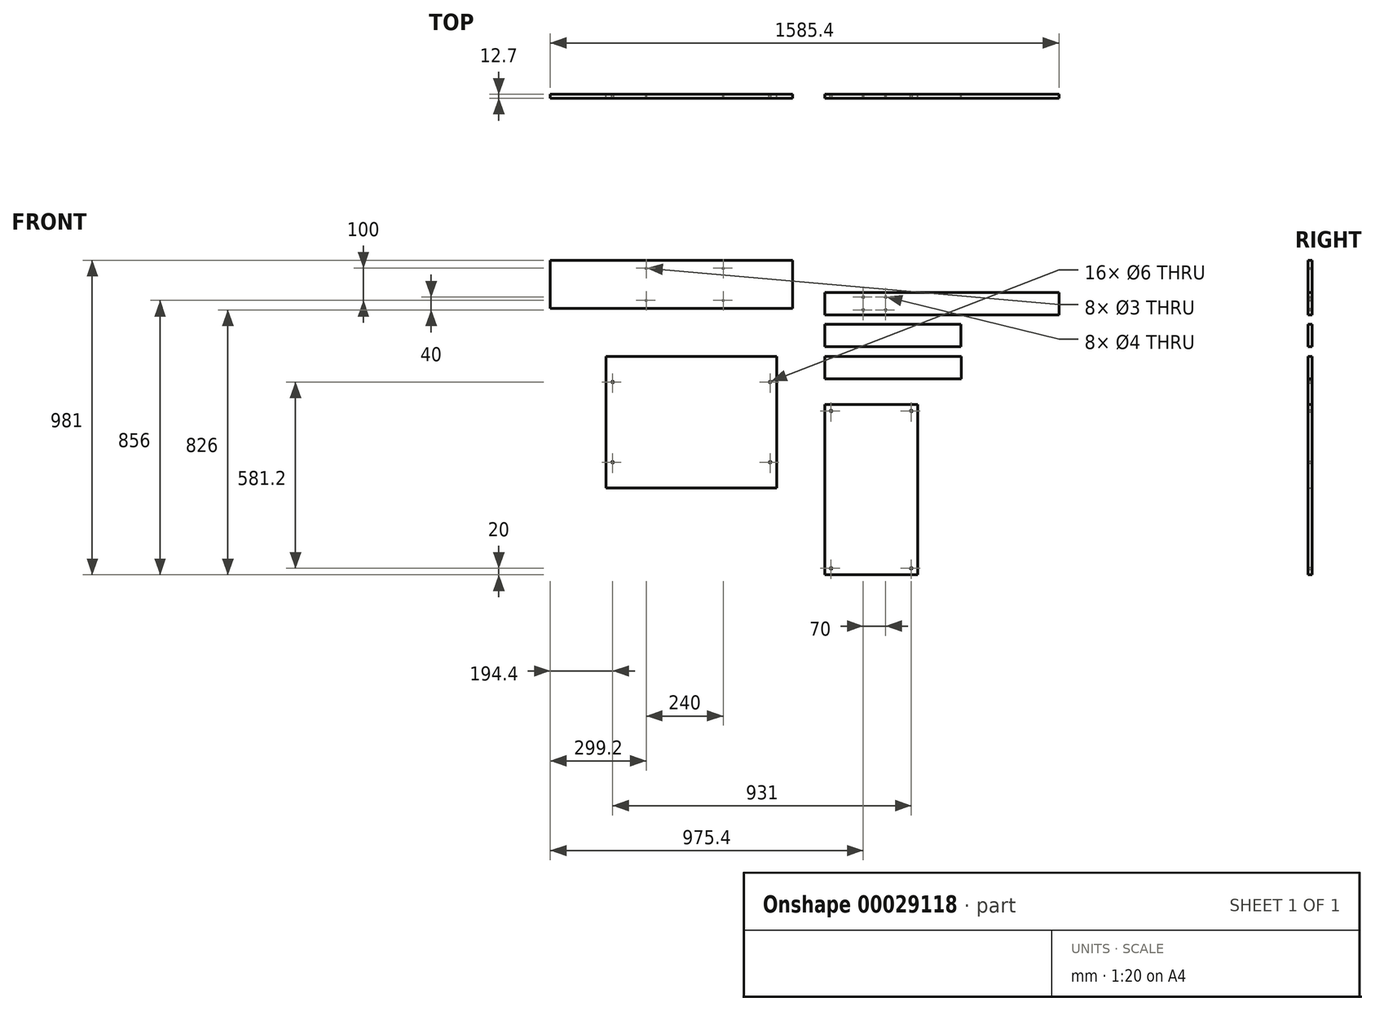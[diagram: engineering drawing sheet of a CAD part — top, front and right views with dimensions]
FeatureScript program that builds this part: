
annotation { "Feature Type Name" : "Feature", "Feature Type Description" : "" }
export const myFeature = defineFeature(function(context is Context, id is Id, definition is map)
    precondition{}
    {
        {
            var Q0;
            Q0=qCreatedBy(makeId("Front.planeOp"),FACE);
            var sketch = newSketch(context, id + "F0", { "sketchPlane" : qUnion([Q0])});
            skLineSegment(sketch, "E0.bottom", {"start": v(50, 100) * mm, "end": v(780, 100) * mm});
            skLineSegment(sketch, "E0.top", {"start": v(50, 30) * mm, "end": v(780, 30) * mm});
            skLineSegment(sketch, "E0.left", {"start": v(50, 100) * mm, "end": v(50, 30) * mm});
            skLineSegment(sketch, "E0.right", {"start": v(780, 100) * mm, "end": v(780, 30) * mm});
            skLineSegment(sketch, "E1", {"start": v(170, 85) * mm, "end": v(240, 45) * mm, "construction": true});
            skPoint(sketch, "E2", {"position": v(205, 65) * mm});
            skCircle(sketch, "E3", {"center": v(240, 85) * mm, "radius": 2 * mm});
            skCircle(sketch, "E4", {"center": v(170, 45) * mm, "radius": 2 * mm});
            skCircle(sketch, "E5", {"center": v(170, 85) * mm, "radius": 2 * mm});
            skCircle(sketch, "E6", {"center": v(240, 45) * mm, "radius": 2 * mm});
            skLineSegment(sketch, "E7", {"start": v(50, 30) * mm, "end": v(780, 100) * mm, "construction": true});
            skPoint(sketch, "E8", {"position": v(415, 65) * mm});
            skSolve(sketch);
        }
        {
            var Q0;
            Q0 = qSketchRegion(id + "F0", true);
            extrude(context, id + "F1", {"entities" : qUnion([Q0]), "depth" : 12.7 * mm});
        }
        {
            var Q0;
            Q0=qCreatedBy(makeId("Front.planeOp"),FACE);
            var sketch = newSketch(context, id + "F2", { "sketchPlane" : qUnion([Q0])});
            skLineSegment(sketch, "E9.bottom", {"start": v(50, 0) * mm, "end": v(474.6, 0) * mm});
            skLineSegment(sketch, "E9.top", {"start": v(50, -70) * mm, "end": v(474.6, -70) * mm});
            skLineSegment(sketch, "E9.left", {"start": v(50, 0) * mm, "end": v(50, -70) * mm});
            skLineSegment(sketch, "E9.right", {"start": v(474.6, 0) * mm, "end": v(474.6, -70) * mm});
            skSolve(sketch);
        }
        {
            var Q0;
            Q0 = qSketchRegion(id + "F2", true);
            extrude(context, id + "F3", {"entities" : qUnion([Q0]), "depth" : 12.7 * mm});
        }
        {
            var Q0;
            Q0=qCreatedBy(makeId("Front.planeOp"),FACE);
            var sketch = newSketch(context, id + "F4", { "sketchPlane" : qUnion([Q0])});
            skLineSegment(sketch, "E10.bottom", {"start": v(50.92, -100) * mm, "end": v(475.52, -100) * mm});
            skLineSegment(sketch, "E10.top", {"start": v(50.92, -170) * mm, "end": v(475.52, -170) * mm});
            skLineSegment(sketch, "E10.left", {"start": v(50.92, -100) * mm, "end": v(50.92, -170) * mm});
            skLineSegment(sketch, "E10.right", {"start": v(475.52, -100) * mm, "end": v(475.52, -170) * mm});
            skSolve(sketch);
        }
        {
            var Q0;
            Q0=makeQuery(id+"F4.imprint","IMPRINT",FACE,{"disambiguationData":[TD([[makeQuery(id+"F4.imprint","IMPRINT",EDGE,{"derivedFrom":sQuery(id+"F4.wireOp",EDGE,"E10.bottom")}),-1.0]])]});
            extrude(context, id + "F5", {"entities" : qUnion([Q0]), "depth" : 12.7 * mm});
        }
        {
            var Q0;
            Q0=qCreatedBy(makeId("Front.planeOp"),FACE);
            var sketch = newSketch(context, id + "F6", { "sketchPlane" : qUnion([Q0])});
            skLineSegment(sketch, "E11.bottom", {"start": v(-50, 50) * mm, "end": v(-805.4, 50) * mm});
            skLineSegment(sketch, "E11.top", {"start": v(-50, 200) * mm, "end": v(-805.4, 200) * mm});
            skLineSegment(sketch, "E11.left", {"start": v(-50, 50) * mm, "end": v(-50, 200) * mm});
            skLineSegment(sketch, "E11.right", {"start": v(-805.4, 50) * mm, "end": v(-805.4, 200) * mm});
            skCircle(sketch, "E12", {"center": v(-506.2, 75) * mm, "radius": 1.5 * mm});
            skCircle(sketch, "E13", {"center": v(-266.2, 175) * mm, "radius": 1.5 * mm});
            skCircle(sketch, "E14", {"center": v(-506.2, 175) * mm, "radius": 1.5 * mm});
            skCircle(sketch, "E15", {"center": v(-266.2, 75) * mm, "radius": 1.5 * mm});
            skLineSegment(sketch, "E16", {"start": v(-506.2, 75) * mm, "end": v(-266.2, 175) * mm, "construction": true});
            skPoint(sketch, "E17", {"position": v(-386.2, 125) * mm});
            skLineSegment(sketch, "E18", {"start": v(-805.4, 200) * mm, "end": v(-50, 50) * mm, "construction": true});
            skPoint(sketch, "E19", {"position": v(-427.7, 125) * mm});
            skSolve(sketch);
        }
        {
            var Q0;
            Q0=makeQuery(id+"F6.imprint","IMPRINT",FACE,{"disambiguationData":[TD([[makeQuery(id+"F6.imprint","IMPRINT",EDGE,{"derivedFrom":sQuery(id+"F6.wireOp",EDGE,"E11.bottom")}),-1.0]])]});
            extrude(context, id + "F7", {"entities" : qUnion([Q0]), "depth" : 12.7 * mm});
        }
        {
            var Q0;
            Q0=qCreatedBy(makeId("Front.planeOp"),FACE);
            var sketch = newSketch(context, id + "F8", { "sketchPlane" : qUnion([Q0])});
            skLineSegment(sketch, "E20.bottom", {"start": v(-100, -100) * mm, "end": v(-631, -100) * mm});
            skLineSegment(sketch, "E20.top", {"start": v(-100, -509.6) * mm, "end": v(-631, -509.6) * mm});
            skLineSegment(sketch, "E20.left", {"start": v(-100, -100) * mm, "end": v(-100, -509.6) * mm});
            skLineSegment(sketch, "E20.right", {"start": v(-631, -100) * mm, "end": v(-631, -509.6) * mm});
            skCircle(sketch, "E21", {"center": v(-120, -429.8) * mm, "radius": 3 * mm});
            skCircle(sketch, "E22", {"center": v(-611, -179.8) * mm, "radius": 3 * mm});
            skCircle(sketch, "E23", {"center": v(-120, -179.8) * mm, "radius": 3 * mm});
            skCircle(sketch, "E24", {"center": v(-611, -429.8) * mm, "radius": 3 * mm});
            skLineSegment(sketch, "E25", {"start": v(-611, -179.8) * mm, "end": v(-120, -429.8) * mm, "construction": true});
            skPoint(sketch, "E26", {"position": v(-365.5, -304.8) * mm});
            skLineSegment(sketch, "E27", {"start": v(-100, -100) * mm, "end": v(-631, -509.6) * mm, "construction": true});
            skSolve(sketch);
        }
        {
            var Q0;
            Q0=makeQuery(id+"F8.imprint","IMPRINT",FACE,{"disambiguationData":[TD([[makeQuery(id+"F8.imprint","IMPRINT",EDGE,{"derivedFrom":sQuery(id+"F8.wireOp",EDGE,"E20.bottom")}),1.0]])]});
            extrude(context, id + "F9", {"entities" : qUnion([Q0]), "depth" : 12.7 * mm});
        }
        {
            var Q0;
            Q0=qCreatedBy(makeId("Front.planeOp"),FACE);
            var sketch = newSketch(context, id + "F10", { "sketchPlane" : qUnion([Q0])});
            skLineSegment(sketch, "E28.bottom", {"start": v(50, -250) * mm, "end": v(340, -250) * mm});
            skLineSegment(sketch, "E28.top", {"start": v(50, -781) * mm, "end": v(340, -781) * mm});
            skLineSegment(sketch, "E28.left", {"start": v(50, -250) * mm, "end": v(50, -781) * mm});
            skLineSegment(sketch, "E28.right", {"start": v(340, -250) * mm, "end": v(340, -781) * mm});
            skLineSegment(sketch, "E29", {"start": v(50, -250) * mm, "end": v(340, -781) * mm, "construction": true});
            skPoint(sketch, "E30", {"position": v(195, -515.5) * mm});
            skCircle(sketch, "E31", {"center": v(70, -270) * mm, "radius": 3 * mm});
            skCircle(sketch, "E32", {"center": v(320, -270) * mm, "radius": 3 * mm});
            skCircle(sketch, "E33", {"center": v(320, -761) * mm, "radius": 3 * mm});
            skCircle(sketch, "E34", {"center": v(70, -761) * mm, "radius": 3 * mm});
            skSolve(sketch);
        }
        {
            var Q0;
            Q0 = qSketchRegion(id + "F10", true);
            extrude(context, id + "F11", {"entities" : qUnion([Q0]), "depth" : 12.7 * mm});
        }
    });
